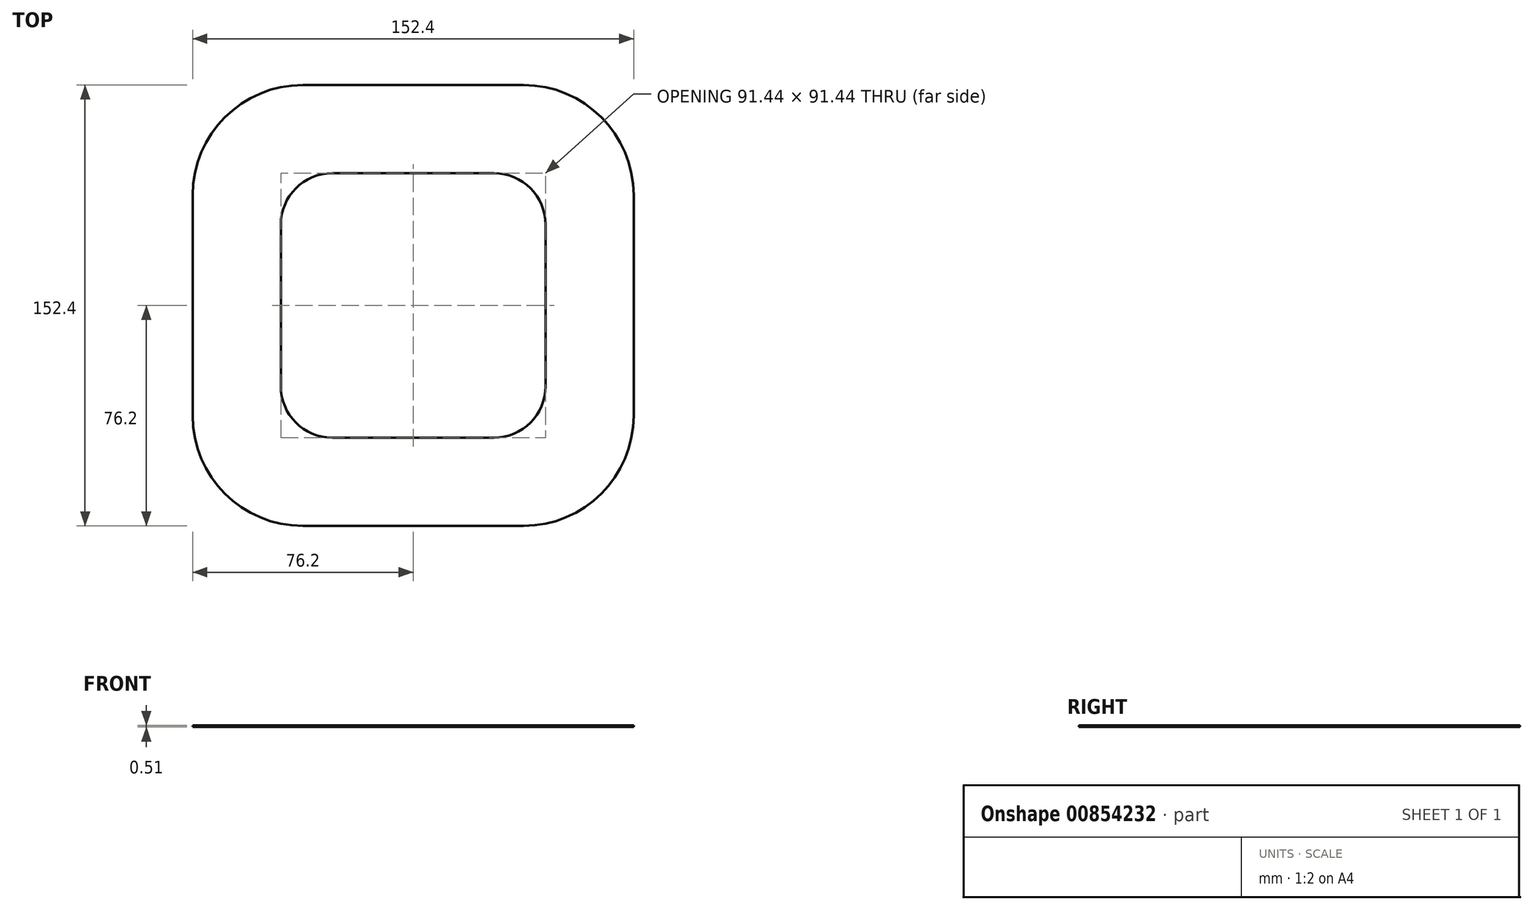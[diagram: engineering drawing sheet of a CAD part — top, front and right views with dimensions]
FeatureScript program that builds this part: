
annotation { "Feature Type Name" : "Feature", "Feature Type Description" : "" }
export const myFeature = defineFeature(function(context is Context, id is Id, definition is map)
    precondition{}
    {
        {
            var Q0;
            Q0=qCreatedBy(makeId("Top.planeOp"),FACE);
            var sketch = newSketch(context, id + "F0", { "sketchPlane" : qUnion([Q0])});
            skLineSegment(sketch, "E0.bottom", {"start": v(38.1, 76.2) * mm, "end": v(-38.1, 76.2) * mm});
            skLineSegment(sketch, "E0.top", {"start": v(38.1, -76.2) * mm, "end": v(-38.1, -76.2) * mm});
            skLineSegment(sketch, "E0.left", {"start": v(76.2, 38.1) * mm, "end": v(76.2, -38.1) * mm});
            skLineSegment(sketch, "E0.right", {"start": v(-76.2, 38.1) * mm, "end": v(-76.2, -38.1) * mm});
            skPoint(sketch, "E0.middle", {"position": v(0, 0) * mm});
            skPoint(sketch, "E1.visualSharp", {"position": v(-76.2, 76.2) * mm});
            skArc(sketch, "E1.filletArc", {"start": v(-38.1, 76.2) * mm, "mid": v(-65.04, 65.04) * mm, "end": v(-76.2, 38.1) * mm});
            skPoint(sketch, "E2.visualSharp", {"position": v(76.2, 76.2) * mm});
            skArc(sketch, "E2.filletArc", {"start": v(76.2, 38.1) * mm, "mid": v(65.04, 65.04) * mm, "end": v(38.1, 76.2) * mm});
            skPoint(sketch, "E3.visualSharp", {"position": v(76.2, -76.2) * mm});
            skArc(sketch, "E3.filletArc", {"start": v(38.1, -76.2) * mm, "mid": v(65.04, -65.04) * mm, "end": v(76.2, -38.1) * mm});
            skPoint(sketch, "E4.visualSharp", {"position": v(-76.2, -76.2) * mm});
            skArc(sketch, "E4.filletArc", {"start": v(-76.2, -38.1) * mm, "mid": v(-65.04, -65.04) * mm, "end": v(-38.1, -76.2) * mm});
            skLineSegment(sketch, "E5.bottom", {"start": v(27.94, 45.72) * mm, "end": v(-27.94, 45.72) * mm});
            skLineSegment(sketch, "E5.top", {"start": v(27.94, -45.72) * mm, "end": v(-27.94, -45.72) * mm});
            skLineSegment(sketch, "E5.left", {"start": v(45.72, 27.94) * mm, "end": v(45.72, -27.94) * mm});
            skLineSegment(sketch, "E5.right", {"start": v(-45.72, 27.94) * mm, "end": v(-45.72, -27.94) * mm});
            skPoint(sketch, "E6.visualSharp", {"position": v(-45.72, 45.72) * mm});
            skArc(sketch, "E6.filletArc", {"start": v(-27.94, 45.72) * mm, "mid": v(-40.51, 40.51) * mm, "end": v(-45.72, 27.94) * mm});
            skPoint(sketch, "E7.visualSharp", {"position": v(45.72, 45.72) * mm});
            skArc(sketch, "E7.filletArc", {"start": v(45.72, 27.94) * mm, "mid": v(40.51, 40.51) * mm, "end": v(27.94, 45.72) * mm});
            skPoint(sketch, "E8.visualSharp", {"position": v(45.72, -45.72) * mm});
            skArc(sketch, "E8.filletArc", {"start": v(27.94, -45.72) * mm, "mid": v(40.51, -40.51) * mm, "end": v(45.72, -27.94) * mm});
            skPoint(sketch, "E9.visualSharp", {"position": v(-45.72, -45.72) * mm});
            skArc(sketch, "E9.filletArc", {"start": v(-45.72, -27.94) * mm, "mid": v(-40.51, -40.51) * mm, "end": v(-27.94, -45.72) * mm});
            skSolve(sketch);
        }
        {
            var Q0;
            Q0 = qSketchRegion(id + "F0", true);
            extrude(context, id + "F1", {"entities" : qUnion([Q0]), "depth" : 0.5 * mm, "offsetDistance" : 25.4 * mm});
        }
    });
